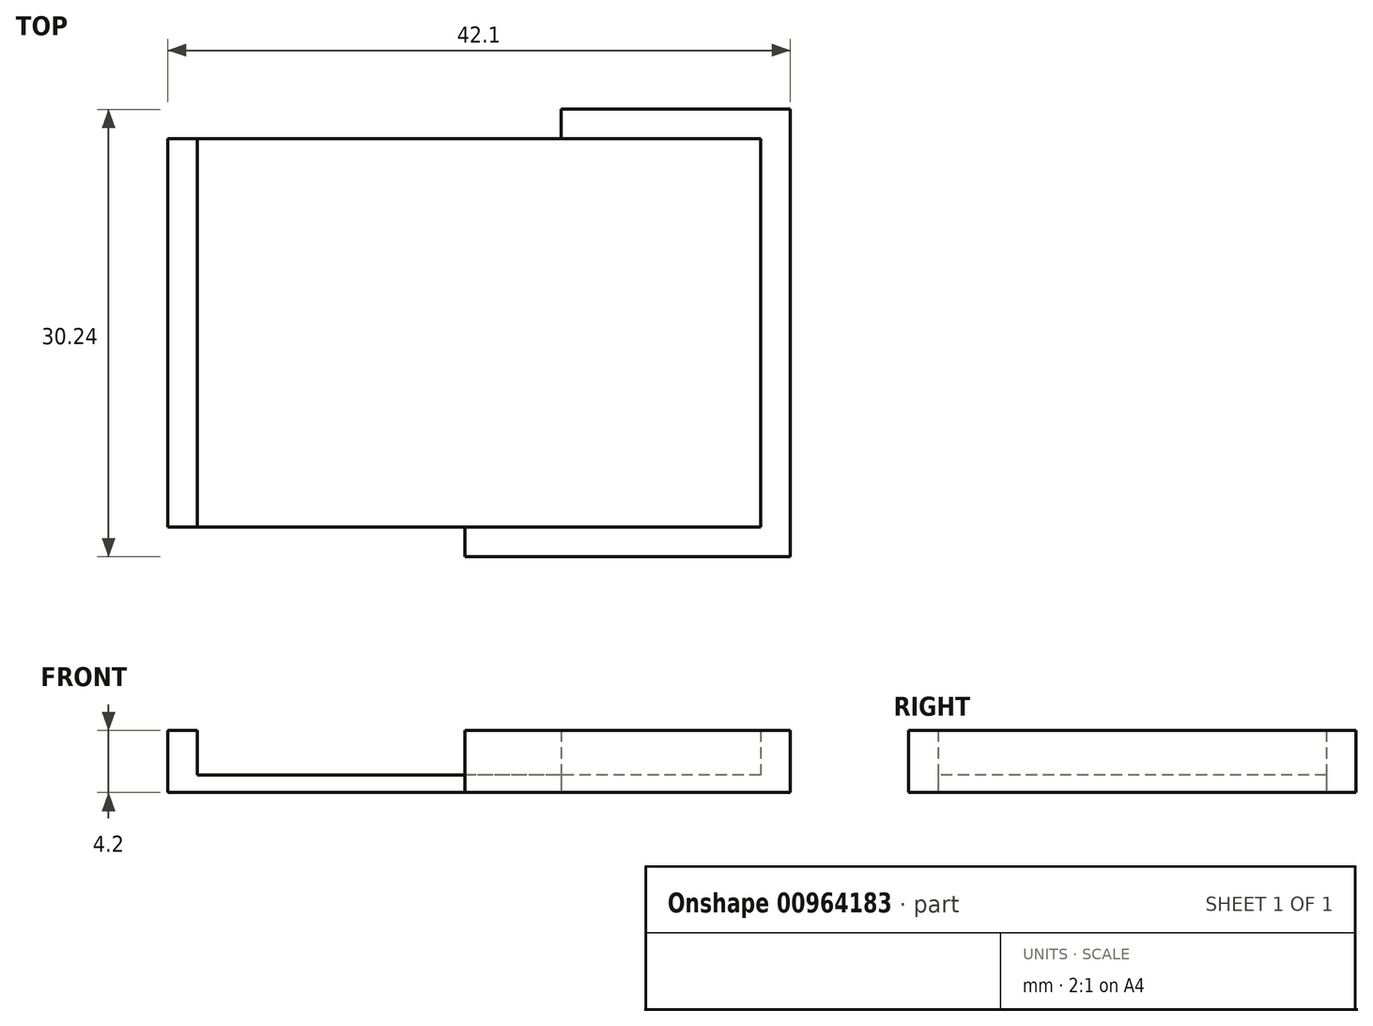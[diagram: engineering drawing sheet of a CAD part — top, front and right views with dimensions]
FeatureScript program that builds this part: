
annotation { "Feature Type Name" : "Feature", "Feature Type Description" : "" }
export const myFeature = defineFeature(function(context is Context, id is Id, definition is map)
    precondition{}
    {
        {
            var Q0;
            Q0=qCreatedBy(makeId("Top.planeOp"),FACE);
            var sketch = newSketch(context, id + "F0", { "sketchPlane" : qUnion([Q0])});
            skLineSegment(sketch, "E0.bottom", {"start": v(21.05, 15.12) * mm, "end": v(-21.05, 15.13) * mm});
            skLineSegment(sketch, "E0.top", {"start": v(21.05, -15.13) * mm, "end": v(-21.05, -15.12) * mm});
            skLineSegment(sketch, "E0.left", {"start": v(21.05, 15.12) * mm, "end": v(21.05, -15.13) * mm});
            skLineSegment(sketch, "E0.right", {"start": v(-21.05, 15.12) * mm, "end": v(-21.05, -15.12) * mm});
            skPoint(sketch, "E0.middle", {"position": v(0, 0) * mm});
            skLineSegment(sketch, "E1.0", {"start": v(19.05, 13.12) * mm, "end": v(-19.05, 13.13) * mm});
            skLineSegment(sketch, "E1.1", {"start": v(19.05, 13.12) * mm, "end": v(19.05, -13.13) * mm});
            skLineSegment(sketch, "E1.2", {"start": v(19.05, -13.13) * mm, "end": v(-19.05, -13.12) * mm});
            skLineSegment(sketch, "E1.3", {"start": v(-19.05, 13.13) * mm, "end": v(-19.05, -13.12) * mm});
            skLineSegment(sketch, "E2.bottom", {"start": v(0.55, 13.12) * mm, "end": v(5.55, 13.12) * mm});
            skLineSegment(sketch, "E2.top", {"start": v(0.55, 15.13) * mm, "end": v(5.55, 15.13) * mm});
            skLineSegment(sketch, "E2.left", {"start": v(0.55, 13.12) * mm, "end": v(0.55, 15.12) * mm});
            skLineSegment(sketch, "E2.right", {"start": v(5.55, 13.12) * mm, "end": v(5.55, 15.12) * mm});
            skLineSegment(sketch, "E3", {"start": v(-19.05, -13.12) * mm, "end": v(-21.05, -13.12) * mm});
            skLineSegment(sketch, "E4", {"start": v(-19.05, 13.13) * mm, "end": v(-21.05, 13.13) * mm});
            skLineSegment(sketch, "E5", {"start": v(-0.95, -13.13) * mm, "end": v(-0.95, -15.13) * mm});
            skSolve(sketch);
        }
        {
            var Q0;
            {var subQ3=sQuery(id+"F0.wireOp",EDGE,"E0.left");Q0=makeQuery(id+"F0.imprint","IMPRINT",FACE,{"disambiguationData":[TD([[makeQuery(id+"F0.imprint","IMPRINT",EDGE,{"derivedFrom":subQ3}),-1.0]])]});}
            var Q1;
            Q1=makeQuery(id+"F0.imprint","IMPRINT",FACE,{"disambiguationData":[TD([[makeQuery(id+"F0.imprint","IMPRINT",EDGE,{"derivedFrom":sQuery(id+"F0.wireOp",EDGE,"E1.3")}),-1.0]])]});
            extrude(context, id + "F1", {"entities" : qUnion([Q0, Q1]), "depth" : 4.2 * mm, "offsetDistance" : 25 * mm});
        }
        {
            var Q0;
            {var subQ0=sQuery(id+"F0.wireOp",EDGE,"E1.1");Q0=makeQuery(id+"F0.imprint","IMPRINT",FACE,{"disambiguationData":[TD([[makeQuery(id+"F0.imprint","IMPRINT",EDGE,{"derivedFrom":subQ0}),-1.0]])]});}
            extrude(context, id + "F2", {"entities" : qUnion([Q0]), "operationType" : NewBodyOperationType.ADD, "depth" : 1.2 * mm, "offsetDistance" : 25 * mm});
        }
    });
